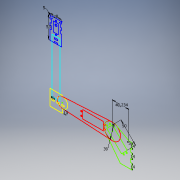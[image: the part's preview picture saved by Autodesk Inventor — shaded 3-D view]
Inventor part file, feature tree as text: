
AUTODESK INVENTOR PART (.ipt)
format: ipt  version: 2018 (Build 220112000, 112)  size: 130,560 bytes
history: native  units: mm
features: sketch x1
ambient origin geometry x8: Origin, YZ Plane, XZ Plane, XY Plane, X Axis, Y Axis, Z Axis, Center Point
feature tree (1):
  sketch  "Boceto1"  dims[d15=39.0mm d17=3.0mm d21=14.0mm d22=14.0mm d25=14.0mm d26=30.0mm d29=40.234376mm d30=50.0mm d45=6.0mm d62=10.0mm d94=53.0mm d95=28.0mm d102=5.0mm]
